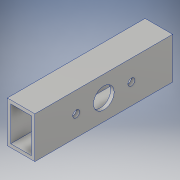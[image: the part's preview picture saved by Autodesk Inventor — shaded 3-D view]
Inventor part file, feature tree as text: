
AUTODESK INVENTOR PART (.ipt)
format: ipt  version: 2017 (Build 210142000, 142)  size: 125,952 bytes
history: native  units: in
note: dims shown in document units (in); Inventor stores cm internally (conversion verified against a paired STEP export)
features: extrude x2, hole x2, sketch x2, pattern_linear x1
ambient origin geometry x8: Origin, YZ Plane, XZ Plane, XY Plane, X Axis, Y Axis, Z Axis, Center Point
bodies: Solid1 (feature_tree)
feature tree (7):
  extrude  "Extrusion1"  Depth=1.5in
  extrude  "Extrusion2"  Depth=5.0in TaperAngle=0.0deg
  pattern_linear  "Rectangular Pattern1"  Spacing1=0.25in  [1 undecoded]
  hole  "Hole1"  [1 undecoded]
  hole  "Hole2"  [1 undecoded]
  sketch  "Sketch1"  dims[d0=1.0in d1=1.5in]
  sketch  "Sketch2"  dims[d2=0.125in d3=5.0in d4=0.0in d5=0.25in d6=5.0in d7=0.0in d8=1.5748in d10=1.0in d11=1.0in d12=1.0in d13=0.625in d14=0.75in d15=0.375in d16=0.25in d17=0.5635in d18=1.0in d19=0.8108in d20=1.0in d21=1.0in d22=0.75in d23=0.75in d24=0.375in d25=0.25in d26=0.5635in d27=1.0in d28=0.8108in]
note: 3 required parameter values undecoded (feature->parameter linkage not recoverable at this tier; creation-order binding heuristic only, values carry confidence <= 0.55)
